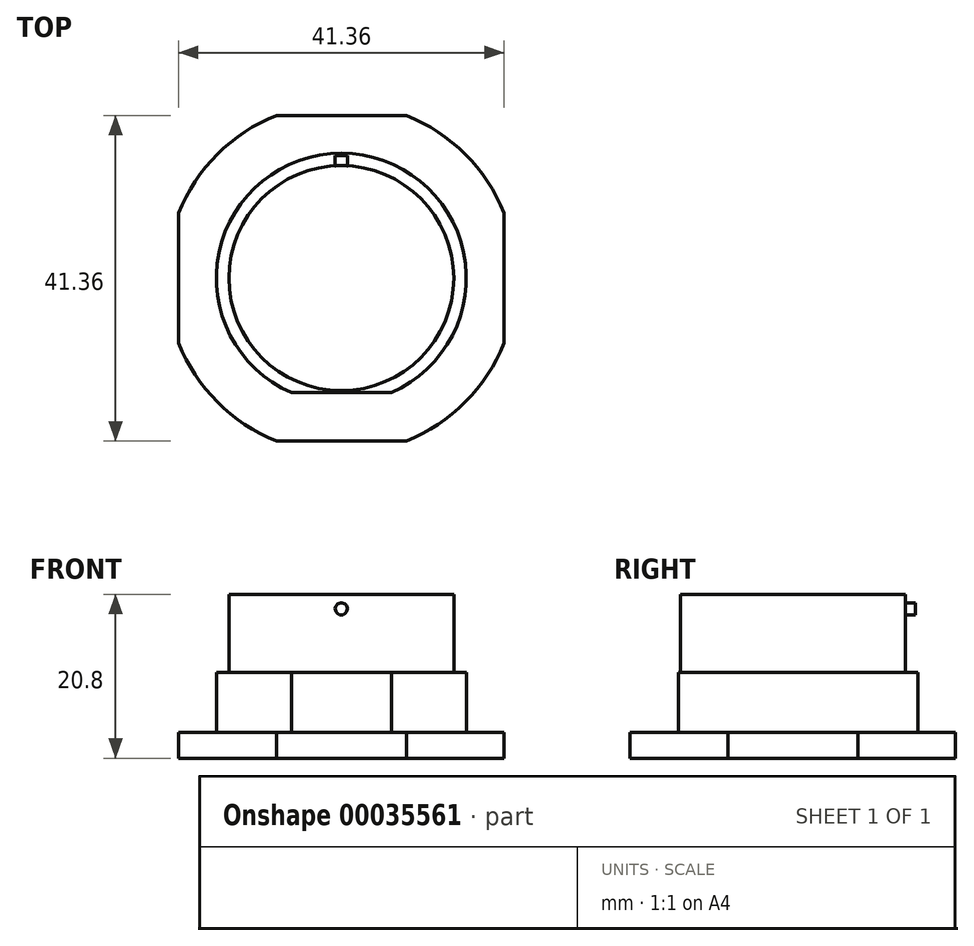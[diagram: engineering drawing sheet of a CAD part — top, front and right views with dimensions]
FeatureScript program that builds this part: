
annotation { "Feature Type Name" : "Feature", "Feature Type Description" : "" }
export const myFeature = defineFeature(function(context is Context, id is Id, definition is map)
    precondition{}
    {
        {
            var Q0;
            Q0=qCreatedBy(makeId("Top.planeOp"),FACE);
            var sketch = newSketch(context, id + "F0", { "sketchPlane" : qUnion([Q0])});
            skLineSegment(sketch, "E0.rect.bottom", {"start": v(-8.26, 20.68) * mm, "end": v(8.26, 20.68) * mm});
            skLineSegment(sketch, "E0.rect.top", {"start": v(-8.26, -20.68) * mm, "end": v(8.26, -20.68) * mm});
            skLineSegment(sketch, "E0.rect.left", {"start": v(-20.68, 8.26) * mm, "end": v(-20.68, -8.26) * mm});
            skLineSegment(sketch, "E0.rect.right", {"start": v(20.68, 8.26) * mm, "end": v(20.68, -8.26) * mm});
            skPoint(sketch, "E0.rect.middle", {"position": v(0, 0) * mm});
            skArc(sketch, "E1", {"start": v(-8.26, 20.68) * mm, "mid": v(-15.74, 15.74) * mm, "end": v(-20.68, 8.26) * mm});
            skPoint(sketch, "E2.orphan", {"position": v(-20.68, 20.68) * mm});
            skPoint(sketch, "E3.orphan", {"position": v(20.68, 20.68) * mm});
            skArc(sketch, "E4.trimOffspring", {"start": v(20.68, 8.26) * mm, "mid": v(15.74, 15.74) * mm, "end": v(8.26, 20.68) * mm});
            skArc(sketch, "E5.trimOffspring", {"start": v(-20.68, -8.26) * mm, "mid": v(-15.74, -15.74) * mm, "end": v(-8.26, -20.68) * mm});
            skPoint(sketch, "E6.orphan", {"position": v(-20.68, -20.68) * mm});
            skArc(sketch, "E7.trimOffspring", {"start": v(8.26, -20.68) * mm, "mid": v(15.74, -15.74) * mm, "end": v(20.68, -8.26) * mm});
            skPoint(sketch, "E8.orphan", {"position": v(20.68, -20.68) * mm});
            skSolve(sketch);
        }
        {
            var Q0;
            Q0 = qSketchRegion(id + "F0", true);
            extrude(context, id + "F1", {"entities" : qUnion([Q0]), "depth" : 3.28 * mm});
        }
        {
            var Q0;
            Q0=makeQuery(id+"F1.opExtrude","CAP_FACE",FACE,{"disambiguationData":[OSD([sQuery(id+"F0.wireOp",EDGE,"E0.rect.bottom"),sQuery(id+"F0.wireOp",EDGE,"E0.rect.top"),sQuery(id+"F0.wireOp",EDGE,"E0.rect.left"),sQuery(id+"F0.wireOp",EDGE,"E0.rect.right"),sQuery(id+"F0.wireOp",EDGE,"E1"),sQuery(id+"F0.wireOp",EDGE,"E4.trimOffspring"),sQuery(id+"F0.wireOp",EDGE,"E5.trimOffspring"),sQuery(id+"F0.wireOp",EDGE,"E7.trimOffspring")])],"isStart":false});
            var sketch = newSketch(context, id + "F2", { "sketchPlane" : qUnion([Q0])});
            skArc(sketch, "E9", {"start": v(6.35, -14.55) * mm, "mid": v(0, 15.88) * mm, "end": v(-6.35, -14.55) * mm});
            skLineSegment(sketch, "E10", {"start": v(-6.35, -14.55) * mm, "end": v(6.35, -14.55) * mm});
            skSolve(sketch);
        }
        {
            var Q0;
            Q0 = qSketchRegion(id + "F2", true);
            extrude(context, id + "F3", {"entities" : qUnion([Q0]), "operationType" : NewBodyOperationType.ADD, "depth" : 7.62 * mm});
        }
        {
            var Q0;
            Q0=makeQuery(id+"F3.opExtrude","CAP_FACE",FACE,{"disambiguationData":[OSD([sQuery(id+"F2.wireOp",EDGE,"E9"),sQuery(id+"F2.wireOp",EDGE,"E10")])],"isStart":false});
            var sketch = newSketch(context, id + "F4", { "sketchPlane" : qUnion([Q0])});
            skCircle(sketch, "E11", {"center": v(0, 0) * mm, "radius": 14.29 * mm});
            skSolve(sketch);
        }
        {
            var Q0;
            Q0 = qSketchRegion(id + "F4", true);
            extrude(context, id + "F5", {"entities" : qUnion([Q0]), "operationType" : NewBodyOperationType.ADD, "depth" : 9.9 * mm});
        }
        {
            var Q0;
            Q0=qCreatedBy(makeId("Front.planeOp"),FACE);
            var sketch = newSketch(context, id + "F6", { "sketchPlane" : qUnion([Q0])});
            skCircle(sketch, "E12", {"center": v(0, 18.96) * mm, "radius": 0.77 * mm});
            skSolve(sketch);
        }
        {
            var Q0;
            Q0 = qSketchRegion(id + "F6", true);
            extrude(context, id + "F7", {"entities" : qUnion([Q0]), "operationType" : NewBodyOperationType.ADD, "oppositeDirection" : true, "depth" : 15.56 * mm});
        }
    });
